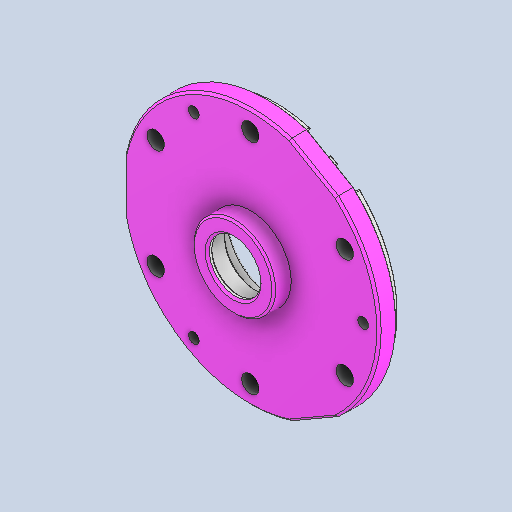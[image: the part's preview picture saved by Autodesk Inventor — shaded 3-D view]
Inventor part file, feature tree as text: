
AUTODESK INVENTOR PART (.ipt)
format: ipt  version: 2024.2 (Build 282272000, 272)  size: 1,143,808 bytes
history: native  units: in
note: dims shown in document units (in); Inventor stores cm internally (conversion verified against a paired STEP export)
features: chamfer x1
ambient origin geometry x8: Origin, YZ Plane, XZ Plane, XY Plane, X Axis, Y Axis, Z Axis, Center Point
bodies: Solid1 (feature_tree)
feature tree (1):
  chamfer  "Chamfer3"  [1 undecoded]
note: 1 required parameter value undecoded (feature->parameter linkage not recoverable at this tier; creation-order binding heuristic only, values carry confidence <= 0.55)
